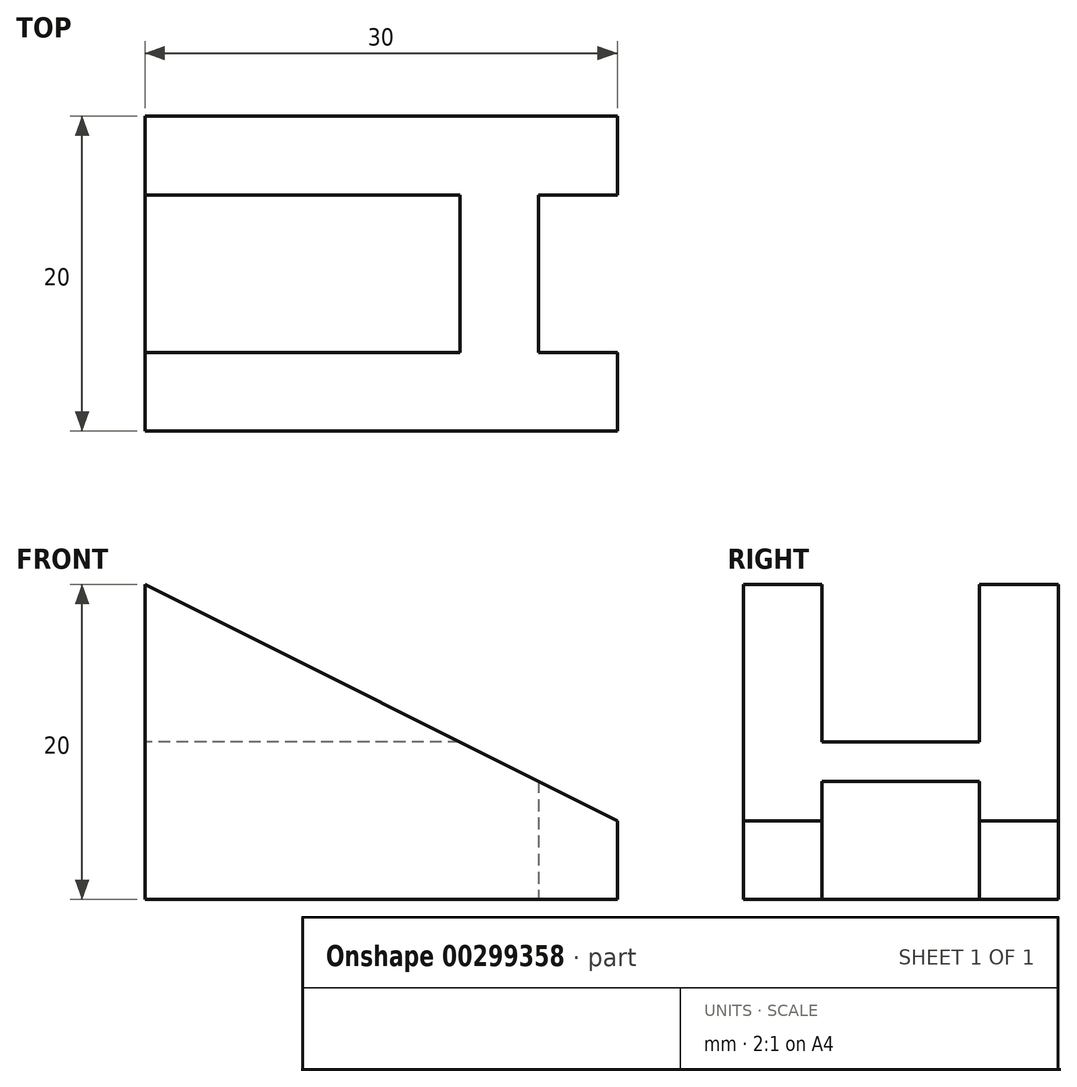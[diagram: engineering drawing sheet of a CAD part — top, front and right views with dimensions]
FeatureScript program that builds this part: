
annotation { "Feature Type Name" : "Feature", "Feature Type Description" : "" }
export const myFeature = defineFeature(function(context is Context, id is Id, definition is map)
    precondition{}
    {
        {
            var Q0;
            Q0=qCreatedBy(makeId("Front.planeOp"),FACE);
            var sketch = newSketch(context, id + "F0", { "sketchPlane" : qUnion([Q0])});
            skLineSegment(sketch, "E0", {"start": v(0, 0) * mm, "end": v(0, 20) * mm});
            skLineSegment(sketch, "E1", {"start": v(0, 20) * mm, "end": v(30, 5) * mm});
            skLineSegment(sketch, "E2", {"start": v(30, 5) * mm, "end": v(30, 0) * mm});
            skLineSegment(sketch, "E3", {"start": v(30, 0) * mm, "end": v(0, 0) * mm});
            skSolve(sketch);
        }
        {
            var Q0;
            Q0 = qSketchRegion(id + "F0", true);
            extrude(context, id + "F1", {"entities" : qUnion([Q0]), "endBound" : BoundingType.SYMMETRIC, "depth" : 20 * mm});
        }
        {
            var Q0;
            Q0=qCreatedBy(makeId("Top.planeOp"),FACE);
            var sketch = newSketch(context, id + "F2", { "sketchPlane" : qUnion([Q0])});
            skLineSegment(sketch, "E4", {"start": v(30, 5) * mm, "end": v(25, 5) * mm});
            skLineSegment(sketch, "E5", {"start": v(25, 5) * mm, "end": v(25, -5) * mm});
            skLineSegment(sketch, "E6", {"start": v(25, -5) * mm, "end": v(30, -5) * mm});
            skLineSegment(sketch, "E7", {"start": v(30, -5) * mm, "end": v(30, 5) * mm});
            skSolve(sketch);
        }
        {
            var Q0;
            Q0 = qSketchRegion(id + "F2", true);
            extrude(context, id + "F3", {"entities" : qUnion([Q0]), "operationType" : NewBodyOperationType.REMOVE, "endBound" : BoundingType.THROUGH_ALL, "depth" : 25 * mm});
        }
        {
            var Q0;
            Q0=qCreatedBy(makeId("Right.planeOp"),FACE);
            var sketch = newSketch(context, id + "F4", { "sketchPlane" : qUnion([Q0])});
            skLineSegment(sketch, "E8.bottom", {"start": v(-5, 20) * mm, "end": v(5, 20) * mm});
            skLineSegment(sketch, "E8.top", {"start": v(-5, 10) * mm, "end": v(5, 10) * mm});
            skLineSegment(sketch, "E8.left", {"start": v(-5, 20) * mm, "end": v(-5, 10) * mm});
            skLineSegment(sketch, "E8.right", {"start": v(5, 20) * mm, "end": v(5, 10) * mm});
            skSolve(sketch);
        }
        {
            var Q0;
            Q0 = qSketchRegion(id + "F4", true);
            extrude(context, id + "F5", {"entities" : qUnion([Q0]), "operationType" : NewBodyOperationType.REMOVE, "endBound" : BoundingType.THROUGH_ALL, "depth" : 25 * mm});
        }
    });
